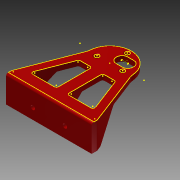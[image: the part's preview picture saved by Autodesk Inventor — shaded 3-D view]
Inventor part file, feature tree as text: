
AUTODESK INVENTOR PART (.ipt)
format: ipt  version: 2013 (Build 170138000, 138)  size: 298,496 bytes
history: native  units: mm
features: fillet x7, sketch x7, chamfer x6, extrude x5, hole x1
ambient origin geometry x8: Origin, YZ Plane, XZ Plane, XY Plane, X Axis, Y Axis, Z Axis, Center Point
feature tree (26):
  extrude  "Extrusion1"  Depth=4.0mm
  extrude  "Extrusion2"  Depth=4.0mm
  fillet  "Fillet1"  Radius=12.0mm
  extrude  "Extrusion3"  Depth=16.5mm
  extrude  "Extrusion4"  Depth=10.0mm
  chamfer  "Chamfer1"  Distance=5.0mm
  extrude  "Extrusion5"  Depth=5.0mm TaperAngle=0.0deg
  chamfer  "Chamfer2"  Distance=5.0mm
  chamfer  "Chamfer3"  Distance=5.0mm
  hole  "Hole1"  [1 undecoded]
  fillet  "Fillet2"  Radius=25.0mm
  fillet  "Fillet3"  Radius=12.156685mm
  fillet  "Fillet4"  Radius=5.0mm
  fillet  "Fillet5"  Radius=25.0mm
  fillet  "Fillet6"  Radius=3.0mm
  fillet  "Fillet7"  Radius=3.0mm
  sketch  "Sketch9"  dims[d44=2.0mm d45=5.0mm d46=5.0mm d47=25.0mm d48=25.0mm d49=12.156685mm d50=5.0mm d51=0.0mm d52=25.0mm d54=3.0mm d55=3.0mm d56=20.0mm d57=0.0mm d58=20.0mm d59=20.0mm d60=45.0deg d61=0.142304mm d62=20.0mm d63=0.0mm d64=20.0mm d65=20.0mm d66=45.0deg d67=20.0mm d68=20.0mm d69=45.0deg d70=25.0mm d71=25.0mm d72=10.0mm d73=10.0mm d74=4.0mm d75=6.0mm d76=4.0mm d77=2.0mm d78=90.0deg d79=8.0mm d80=20.594885mm d81=2.0mm d82=2.0mm d83=2.0mm d84=2.0mm d85=2.0mm d86=2.0mm d87=33.290799mm d88=11.840114mm d89=1.0mm d90=2.0mm d91=45.0deg d92=1.0mm d93=2.0mm d94=45.0deg d95=1.0mm d96=2.0mm d97=45.0deg]
  chamfer  "Chamfer4"  Distance=20.0mm
  chamfer  "Chamfer5"  Distance=20.0mm Angle=45.0deg
  chamfer  "Chamfer6"  Distance=0.142304mm
  sketch  "Sketch1"  dims[d3=40.0mm d4=4.0mm]
  sketch  "Sketch4"  dims[d5=4.0mm d6=4.0mm d7=12.0mm]
  sketch  "Sketch5"  dims[d8=12.0mm d9=16.5mm]
  sketch  "Sketch6"  dims[d10=5.0mm d13=10.0mm]
  sketch  "Sketch7"  dims[d14=3.0mm d38=5.0mm d39=0.0mm]
  sketch  "Sketch8"  dims[d40=25.0mm d42=5.0mm d43=0.0mm]
note: 1 required parameter value undecoded (feature->parameter linkage not recoverable at this tier; creation-order binding heuristic only, values carry confidence <= 0.55)
